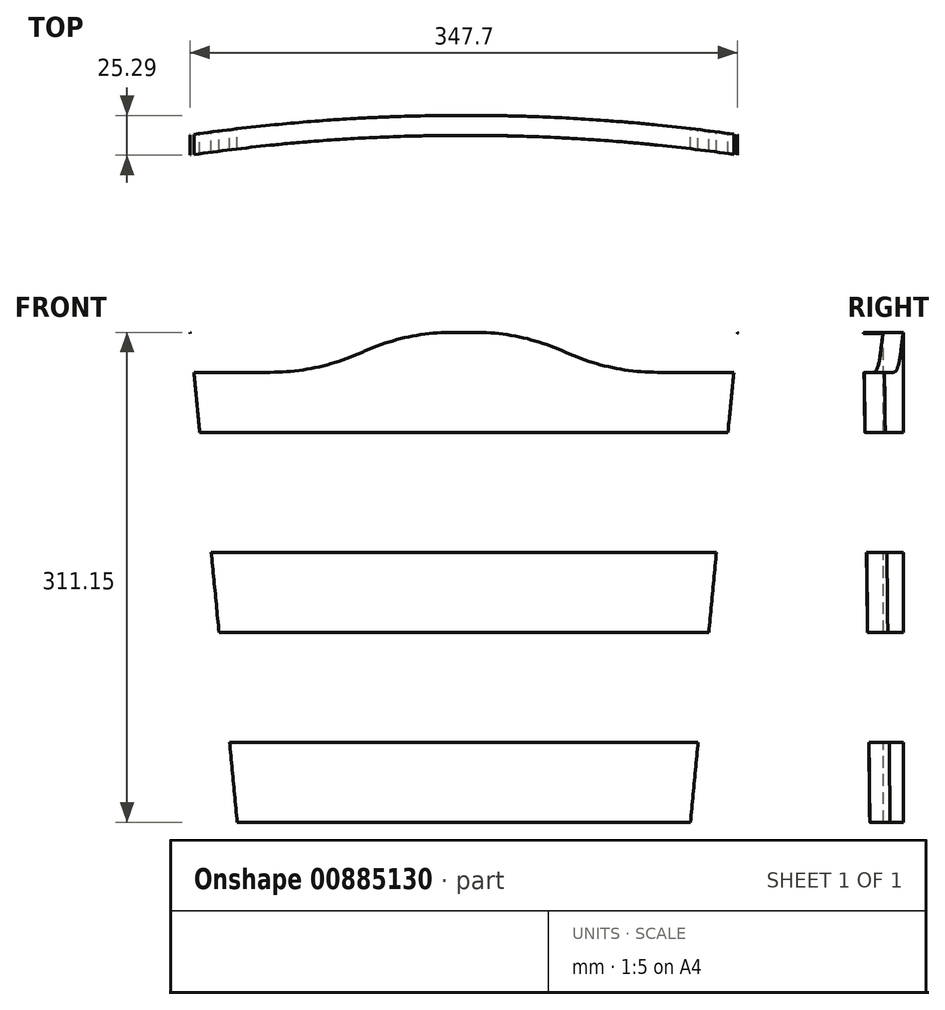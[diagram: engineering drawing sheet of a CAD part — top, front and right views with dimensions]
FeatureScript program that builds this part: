
annotation { "Feature Type Name" : "Feature", "Feature Type Description" : "" }
export const myFeature = defineFeature(function(context is Context, id is Id, definition is map)
    precondition{}
    {
        {
            var Q0;
            Q0=qCreatedBy(makeId("Top.planeOp"),FACE);
            var sketch = newSketch(context, id + "F0", { "sketchPlane" : qUnion([Q0])});
            skArc(sketch, "E0", {"start": v(174.27, 0) * mm, "mid": v(0.42, 12.46) * mm, "end": v(-173.43, 0) * mm, "construction": true});
            skArc(sketch, "E1", {"start": v(173.84, 6.48) * mm, "mid": v(-0.02, 18.8) * mm, "end": v(-173.86, 6.35) * mm});
            skArc(sketch, "E2", {"start": v(173.84, -6.35) * mm, "mid": v(-0.02, 6.1) * mm, "end": v(-173.86, -6.48) * mm});
            skLineSegment(sketch, "E3", {"start": v(-173.86, 6.35) * mm, "end": v(-173.86, -6.48) * mm});
            skLineSegment(sketch, "E4", {"start": v(173.84, 6.48) * mm, "end": v(173.84, -6.35) * mm});
            skSolve(sketch);
        }
        {
            var Q0;
            Q0=makeQuery(id+"F0.imprint","IMPRINT",FACE,{"disambiguationData":[TD([[makeQuery(id+"F0.imprint","IMPRINT",EDGE,{"derivedFrom":sQuery(id+"F0.wireOp",EDGE,"E1")}),1.0]])]});
            extrude(context, id + "F1", {"entities" : qUnion([Q0]), "oppositeDirection" : true, "depth" : 347.66 * mm, "offsetDistance" : 25.4 * mm});
        }
        {
            var Q0;
            Q0=qCreatedBy(makeId("Front.planeOp"),FACE);
            var sketch = newSketch(context, id + "F2", { "sketchPlane" : qUnion([Q0])});
            skLineSegment(sketch, "E5", {"start": v(-173.86, 0) * mm, "end": v(-140.13, -350.3) * mm});
            skLineSegment(sketch, "E6", {"start": v(-140.13, -350.3) * mm, "end": v(-140.13, -350.3) * mm});
            skLineSegment(sketch, "E7", {"start": v(-173.86, -350.3) * mm, "end": v(-140.13, -350.3) * mm});
            skLineSegment(sketch, "E8", {"start": v(-173.86, -350.3) * mm, "end": v(-173.86, 0) * mm});
            skLineSegment(sketch, "E9", {"start": v(0, 0) * mm, "end": v(0, -378.01) * mm, "construction": true});
            skLineSegment(sketch, "E10", {"start": v(0, -378.01) * mm, "end": v(0, -378.01) * mm});
            skLineSegment(sketch, "E11.MirrorCS", {"start": v(173.86, 0) * mm, "end": v(140.13, -350.3) * mm});
            skLineSegment(sketch, "E12.MirrorCS", {"start": v(173.86, -350.3) * mm, "end": v(140.13, -350.3) * mm});
            skLineSegment(sketch, "E13.MirrorCS", {"start": v(173.86, -350.3) * mm, "end": v(173.86, 0) * mm});
            skSolve(sketch);
        }
        {
            var Q0;
            Q0 = qSketchRegion(id + "F2", true);
            extrude(context, id + "F3", {"entities" : qUnion([Q0]), "operationType" : NewBodyOperationType.REMOVE, "endBound" : BoundingType.THROUGH_ALL, "oppositeDirection" : true, "depth" : 25.4 * mm, "offsetDistance" : 25.4 * mm, "hasSecondDirection" : true, "secondDirectionBound" : SecondDirectionBoundingType.THROUGH_ALL, "secondDirectionOppositeDirection" : false, "secondDirectionDepth" : 25.4 * mm});
        }
        {
            var Q0;
            Q0=qCreatedBy(makeId("Front.planeOp"),FACE);
            var sketch = newSketch(context, id + "F4", { "sketchPlane" : qUnion([Q0])});
            skLineSegment(sketch, "E14", {"start": v(123, -25.4) * mm, "end": v(173.8, -25.4) * mm});
            skLineSegment(sketch, "E15", {"start": v(173.8, -25.4) * mm, "end": v(173.8, 0) * mm});
            skLineSegment(sketch, "E16", {"start": v(173.8, 0) * mm, "end": v(0, 0) * mm});
            skLineSegment(sketch, "E17.bottom", {"start": v(-169.3, -139.7) * mm, "end": v(182.69, -139.7) * mm});
            skLineSegment(sketch, "E17.top", {"start": v(-169.3, -63.5) * mm, "end": v(182.69, -63.5) * mm});
            skLineSegment(sketch, "E17.left", {"start": v(-169.3, -139.7) * mm, "end": v(-169.3, -63.5) * mm});
            skLineSegment(sketch, "E17.right", {"start": v(182.69, -139.7) * mm, "end": v(182.69, -63.5) * mm});
            skLineSegment(sketch, "E18.bottom", {"start": v(-170.88, -190.5) * mm, "end": v(174.8, -190.5) * mm});
            skLineSegment(sketch, "E18.top", {"start": v(-170.88, -260.35) * mm, "end": v(174.8, -260.35) * mm});
            skLineSegment(sketch, "E18.left", {"start": v(-170.88, -190.5) * mm, "end": v(-170.88, -260.35) * mm});
            skLineSegment(sketch, "E18.right", {"start": v(174.8, -190.5) * mm, "end": v(174.8, -260.35) * mm});
            skArc(sketch, "E19", {"start": v(6.6, 0) * mm, "mid": v(36.39, -3.21) * mm, "end": v(64.8, -12.7) * mm});
            skArc(sketch, "E20", {"start": v(64.8, -12.7) * mm, "mid": v(93.22, -22.19) * mm, "end": v(123, -25.4) * mm});
            skPoint(sketch, "E21.start.orphan", {"position": v(-173.86, 0) * mm});
            skLineSegment(sketch, "E22", {"start": v(0, 0) * mm, "end": v(0, -21.7) * mm, "construction": true});
            skArc(sketch, "E23.MirrorCS", {"start": v(-6.6, 0) * mm, "mid": v(-36.39, -3.21) * mm, "end": v(-64.8, -12.7) * mm});
            skArc(sketch, "E24.MirrorCS", {"start": v(-64.8, -12.7) * mm, "mid": v(-93.22, -22.19) * mm, "end": v(-123, -25.4) * mm});
            skLineSegment(sketch, "E25.MirrorCS", {"start": v(-123, -25.4) * mm, "end": v(-173.8, -25.4) * mm});
            skLineSegment(sketch, "E26.MirrorCS", {"start": v(-173.8, -25.4) * mm, "end": v(-173.8, 0) * mm});
            skLineSegment(sketch, "E27.MirrorCS", {"start": v(-173.8, 0) * mm, "end": v(0, 0) * mm});
            skLineSegment(sketch, "E28.bottom", {"start": v(-178.84, -311.15) * mm, "end": v(174, -311.15) * mm});
            skLineSegment(sketch, "E28.top", {"start": v(-178.84, -394.1) * mm, "end": v(174, -394.1) * mm});
            skLineSegment(sketch, "E28.left", {"start": v(-178.84, -311.15) * mm, "end": v(-178.84, -394.1) * mm});
            skLineSegment(sketch, "E28.right", {"start": v(174, -311.15) * mm, "end": v(174, -394.1) * mm});
            skSolve(sketch);
        }
        {
            var Q0;
            Q0=makeQuery(id+"F4.imprint","IMPRINT",FACE,{"disambiguationData":[TD([[makeQuery(id+"F4.imprint","IMPRINT",EDGE,{"derivedFrom":sQuery(id+"F4.wireOp",EDGE,"E18.bottom")}),-1.0]])]});
            var Q1;
            Q1=makeQuery(id+"F4.imprint","IMPRINT",FACE,{"disambiguationData":[TD([[makeQuery(id+"F4.imprint","IMPRINT",EDGE,{"derivedFrom":sQuery(id+"F4.wireOp",EDGE,"E17.bottom")}),1.0]])]});
            var Q2;
            Q2=makeQuery(id+"F4.imprint","IMPRINT",FACE,{"disambiguationData":[TD([[makeQuery(id+"F4.imprint","IMPRINT",EDGE,{"derivedFrom":sQuery(id+"F4.wireOp",EDGE,"E14")}),1.0]])]});
            var Q3;
            {var subQ1=sQuery(id+"F4.wireOp",EDGE,"E23.MirrorCS");Q3=makeQuery(id+"F4.imprint","IMPRINT",FACE,{"disambiguationData":[TD([[makeQuery(id+"F4.imprint","IMPRINT",EDGE,{"derivedFrom":subQ1}),-1.0]])]});}
            var Q4;
            Q4=makeQuery(id+"F4.imprint","IMPRINT",FACE,{"disambiguationData":[TD([[makeQuery(id+"F4.imprint","IMPRINT",EDGE,{"derivedFrom":sQuery(id+"F4.wireOp",EDGE,"E28.bottom")}),-1.0]])]});
            extrude(context, id + "F5", {"entities" : qUnion([Q0, Q1, Q2, Q3, Q4]), "operationType" : NewBodyOperationType.REMOVE, "depth" : 76.2 * mm, "offsetDistance" : 25.4 * mm, "hasSecondDirection" : true, "secondDirectionOppositeDirection" : true, "secondDirectionDepth" : 76.2 * mm});
        }
    });
